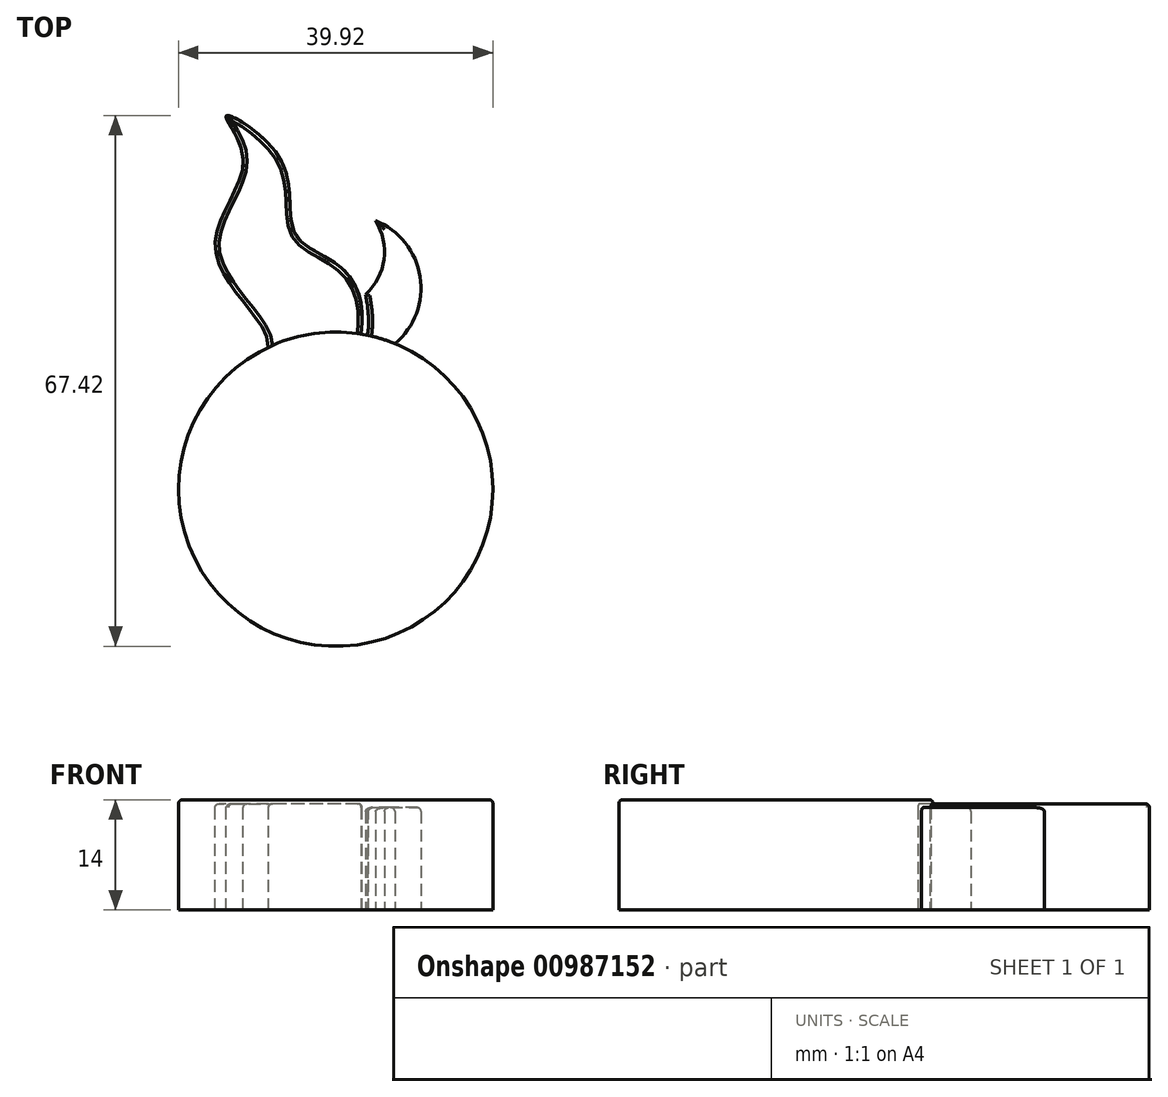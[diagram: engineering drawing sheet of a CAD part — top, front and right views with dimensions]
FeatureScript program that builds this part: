
annotation { "Feature Type Name" : "Feature", "Feature Type Description" : "" }
export const myFeature = defineFeature(function(context is Context, id is Id, definition is map)
    precondition{}
    {
        {
            var Q0;
            Q0=qCreatedBy(makeId("Top.planeOp"),FACE);
            var sketch = newSketch(context, id + "F0", { "sketchPlane" : qUnion([Q0])});
            skCircle(sketch, "E0", {"center": v(0, 0) * mm, "radius": 19.96 * mm});
            skFitSpline(sketch, "E1", {"points": [v(3.24, 19.7) * mm, v(-4.8, 31.85) * mm, v(-6.86, 41.6) * mm, v(-13.89, 47.41) * mm, v(-11.75, 42.03) * mm, v(-15.24, 30.02) * mm, v(-8.58, 18.03) * mm], "startDerivative": vector(17.17, 145.96) * mm, "endDerivative": vector(-9, -43.84) * mm});
            skArc(sketch, "E2", {"start": v(7.53, 18.49) * mm, "mid": v(10.72, 27) * mm, "end": v(5.04, 34.1) * mm});
            skArc(sketch, "E3", {"start": v(3.8, 24.74) * mm, "mid": v(6.13, 29.2) * mm, "end": v(5.04, 34.1) * mm});
            skFitSpline(sketch, "E4", {"points": [v(3.8, 24.74) * mm, v(4.01, 19.56) * mm], "startDerivative": vector(0.72, -4.3) * mm, "endDerivative": vector(-1.09, -4.84) * mm});
            skSolve(sketch);
        }
        {
            var Q0;
            {var subQ0=sQuery(id+"F0.wireOp",EDGE,"E0");var subQ1=makeQuery(id+"F0.imprint","INTERSECT",VERTEX,{"derivedFrom":[subQ0,sQuery(id+"F0.wireOp",EDGE,"E2")]});Q0=makeQuery(id+"F0.imprint","IMPRINT",FACE,{"disambiguationData":[TD([[makeQuery(id+"F0.imprint","IMPRINT",EDGE,{"disambiguationData":[TD([[subQ1,-1.0]])],"derivedFrom":subQ0}),1.0]])]});}
            extrude(context, id + "F1", {"entities" : qUnion([Q0]), "depth" : 4 * mm, "offsetDistance" : 25 * mm});
        }
        {
            var Q0;
            {var subQ0=sQuery(id+"F0.wireOp",EDGE,"E2");Q0=makeQuery(id+"F0.imprint","IMPRINT",FACE,{"disambiguationData":[TD([[makeQuery(id+"F0.imprint","IMPRINT",EDGE,{"derivedFrom":subQ0}),1.0]])]});}
            extrude(context, id + "F2", {"entities" : qUnion([Q0]), "operationType" : NewBodyOperationType.ADD, "depth" : 3 * mm, "offsetDistance" : 25 * mm});
        }
        {
            var Q0;
            {var subQ0=sQuery(id+"F0.wireOp",EDGE,"E1");Q0=makeQuery(id+"F0.imprint","IMPRINT",FACE,{"disambiguationData":[TD([[makeQuery(id+"F0.imprint","IMPRINT",EDGE,{"derivedFrom":subQ0}),1.0]])]});}
            extrude(context, id + "F3", {"entities" : qUnion([Q0]), "operationType" : NewBodyOperationType.ADD, "depth" : 3.5 * mm, "offsetDistance" : 25 * mm});
        }
        {
            var Q0;
            Q0=makeQuery(id+"F3.opExtrude","CAP_EDGE",EDGE,{"disambiguationData":[OSD([sQuery(id+"F0.wireOp",EDGE,"E1")])],"isStart":false});
            var Q1;
            Q1=makeQuery(id+"F3.opExtrude","CAP_EDGE",EDGE,{"disambiguationData":[OSD([sQuery(id+"F0.wireOp",EDGE,"E3")])],"isStart":false});
            var Q2;
            Q2=makeQuery(id+"F3.opExtrude","CAP_EDGE",EDGE,{"disambiguationData":[OSD([sQuery(id+"F0.wireOp",EDGE,"E4")])],"isStart":false});
            var Q3;
            Q3=makeQuery(id+"F3.opExtrude","CAP_EDGE",EDGE,{"disambiguationData":[OSD([sQuery(id+"F0.wireOp",EDGE,"E2")])],"isStart":false});
            var Q4;
            Q4=makeQuery(id+"F1.opExtrude","CAP_EDGE",EDGE,{"disambiguationData":[OSD([sQuery(id+"F0.wireOp",EDGE,"E0")])],"isStart":false});
            var Q5;
            Q5=makeQuery(id+"F2.opExtrude","CAP_EDGE",EDGE,{"disambiguationData":[OSD([sQuery(id+"F0.wireOp",EDGE,"E2")])],"isStart":false});
            var Q6;
            Q6=makeQuery(id+"F2.opExtrude","CAP_EDGE",EDGE,{"disambiguationData":[OSD([sQuery(id+"F0.wireOp",EDGE,"E3")])],"isStart":false});
            var Q7;
            Q7=makeQuery(id+"F2.opExtrude","CAP_EDGE",EDGE,{"disambiguationData":[OSD([sQuery(id+"F0.wireOp",EDGE,"E4")])],"isStart":false});
            fillet(context, id + "F4", {"entities" : qUnion([Q0, Q1, Q2, Q3, Q4, Q5, Q6, Q7]), "radius" : 0.5 * mm, "tangentPropagation" : true, "allowEdgeOverflow" : false});
        }
        {
            var Q0;
            {var subQ0=sQuery(id+"F0.wireOp",EDGE,"E1");var subQ1=sQuery(id+"F0.wireOp",EDGE,"E0");var subQ2=sQuery(id+"F0.wireOp",EDGE,"E4");var subQ3=sQuery(id+"F0.wireOp",EDGE,"E3");var subQ4=sQuery(id+"F0.wireOp",EDGE,"E2");Q0=makeQuery(id+"FJ2AJ5XX3Wwne4g_1.6.F3.boolean.opBoolean","MERGE",FACE,{"derivedFrom":[makeQuery(id+"FJ2AJ5XX3Wwne4g_1.6.F2.boolean.opBoolean","MERGE",FACE,{"derivedFrom":[makeQuery(id+"FJ2AJ5XX3Wwne4g_1.5.F3.boolean.opBoolean","MERGE",FACE,{"derivedFrom":[makeQuery(id+"FJ2AJ5XX3Wwne4g_1.5.F2.boolean.opBoolean","MERGE",FACE,{"derivedFrom":[makeQuery(id+"FJ2AJ5XX3Wwne4g_1.4.F3.boolean.opBoolean","MERGE",FACE,{"derivedFrom":[makeQuery(id+"FJ2AJ5XX3Wwne4g_1.4.F2.boolean.opBoolean","MERGE",FACE,{"derivedFrom":[makeQuery(id+"FJ2AJ5XX3Wwne4g_1.3.F3.boolean.opBoolean","MERGE",FACE,{"derivedFrom":[makeQuery(id+"FJ2AJ5XX3Wwne4g_1.3.F2.boolean.opBoolean","MERGE",FACE,{"derivedFrom":[makeQuery(id+"FJ2AJ5XX3Wwne4g_1.2.F3.boolean.opBoolean","MERGE",FACE,{"derivedFrom":[makeQuery(id+"FJ2AJ5XX3Wwne4g_1.2.F2.boolean.opBoolean","MERGE",FACE,{"derivedFrom":[makeQuery(id+"FJ2AJ5XX3Wwne4g_1.1.F3.boolean.opBoolean","MERGE",FACE,{"derivedFrom":[makeQuery(id+"FJ2AJ5XX3Wwne4g_1.1.F2.boolean.opBoolean","MERGE",FACE,{"derivedFrom":[makeQuery(id+"F3.boolean.opBoolean","MERGE",FACE,{"derivedFrom":[makeQuery(id+"F2.boolean.opBoolean","MERGE",FACE,{"derivedFrom":[makeQuery(id+"F1.opExtrude","CAP_FACE",FACE,{"disambiguationData":[OSD([subQ1])],"isStart":true}),makeQuery(id+"F2.opExtrude","CAP_FACE",FACE,{"disambiguationData":[OSD([subQ1,subQ4,subQ3,subQ2])],"isStart":true})]}),makeQuery(id+"F3.opExtrude","CAP_FACE",FACE,{"disambiguationData":[OSD([subQ1,subQ0])],"isStart":true})]}),makeQuery(id+"FJ2AJ5XX3Wwne4g_1.1.F2.opExtrude","CAP_FACE",FACE,{"disambiguationData":[OSD([subQ1,subQ4,subQ3,subQ2])],"isStart":true})]}),makeQuery(id+"FJ2AJ5XX3Wwne4g_1.1.F3.opExtrude","CAP_FACE",FACE,{"disambiguationData":[OSD([subQ1,subQ0])],"isStart":true})]}),makeQuery(id+"FJ2AJ5XX3Wwne4g_1.2.F2.opExtrude","CAP_FACE",FACE,{"disambiguationData":[OSD([subQ1,subQ4,subQ3,subQ2])],"isStart":true})]}),makeQuery(id+"FJ2AJ5XX3Wwne4g_1.2.F3.opExtrude","CAP_FACE",FACE,{"disambiguationData":[OSD([subQ1,subQ0])],"isStart":true})]}),makeQuery(id+"FJ2AJ5XX3Wwne4g_1.3.F2.opExtrude","CAP_FACE",FACE,{"disambiguationData":[OSD([subQ1,subQ4,subQ3,subQ2])],"isStart":true})]}),makeQuery(id+"FJ2AJ5XX3Wwne4g_1.3.F3.opExtrude","CAP_FACE",FACE,{"disambiguationData":[OSD([subQ1,subQ0])],"isStart":true})]}),makeQuery(id+"FJ2AJ5XX3Wwne4g_1.4.F2.opExtrude","CAP_FACE",FACE,{"disambiguationData":[OSD([subQ1,subQ4,subQ3,subQ2])],"isStart":true})]}),makeQuery(id+"FJ2AJ5XX3Wwne4g_1.4.F3.opExtrude","CAP_FACE",FACE,{"disambiguationData":[OSD([subQ1,subQ0])],"isStart":true})]}),makeQuery(id+"FJ2AJ5XX3Wwne4g_1.5.F2.opExtrude","CAP_FACE",FACE,{"disambiguationData":[OSD([subQ1,subQ4,subQ3,subQ2])],"isStart":true})]}),makeQuery(id+"FJ2AJ5XX3Wwne4g_1.5.F3.opExtrude","CAP_FACE",FACE,{"disambiguationData":[OSD([subQ1,subQ0])],"isStart":true})]}),makeQuery(id+"FJ2AJ5XX3Wwne4g_1.6.F2.opExtrude","CAP_FACE",FACE,{"disambiguationData":[OSD([subQ1,subQ4,subQ3,subQ2])],"isStart":true})]}),makeQuery(id+"FJ2AJ5XX3Wwne4g_1.6.F3.opExtrude","CAP_FACE",FACE,{"disambiguationData":[OSD([subQ1,subQ0])],"isStart":true})]});}
            extrude(context, id + "F5", {"entities" : qUnion([Q0]), "operationType" : NewBodyOperationType.ADD, "depth" : 10 * mm, "offsetDistance" : 25 * mm});
        }
    });
